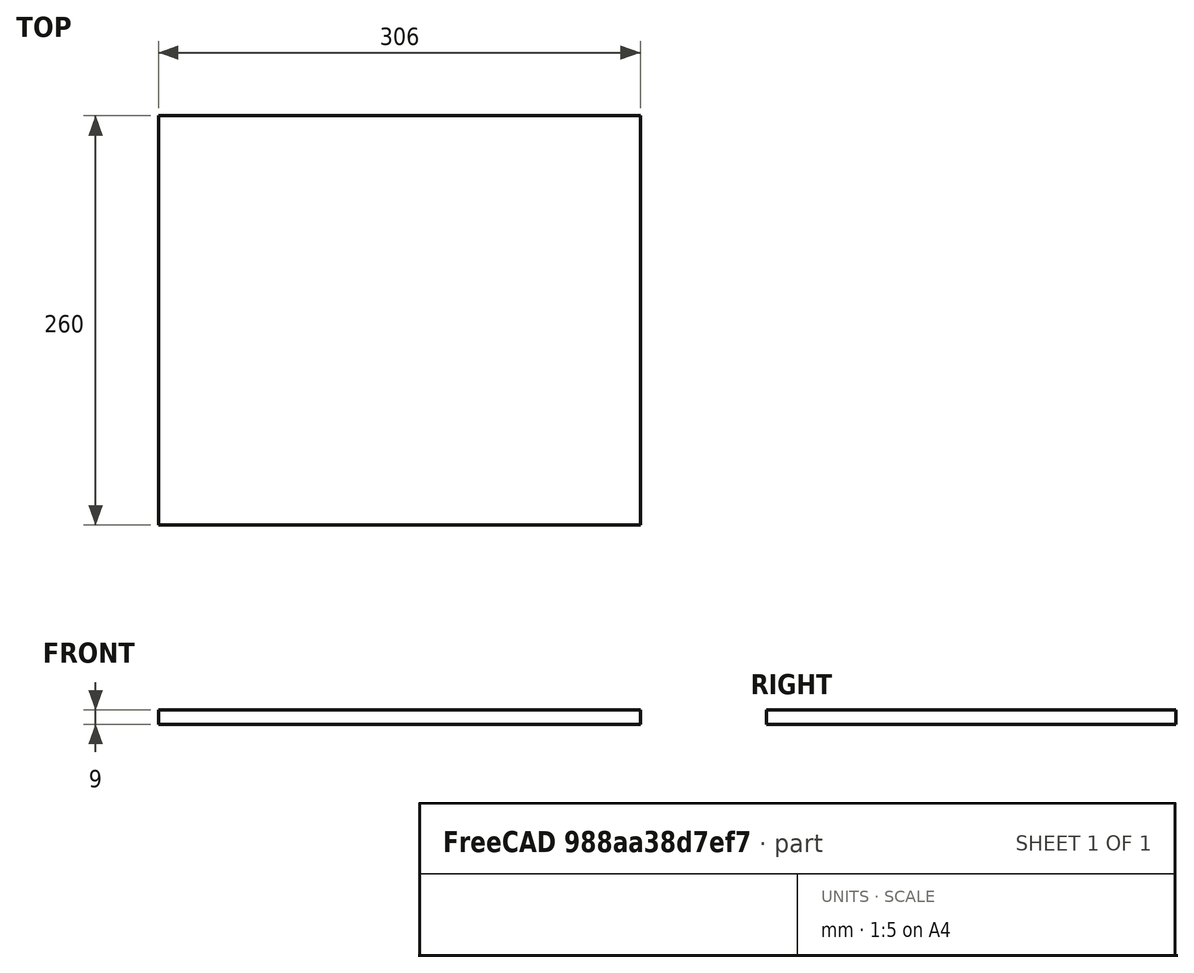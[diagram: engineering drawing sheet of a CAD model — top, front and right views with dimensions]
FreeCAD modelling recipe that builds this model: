
FCSTD DOCUMENT  (FreeCAD 0.16RUnknown)
Label: plaque_av
License: All rights reserved
LicenseURL: http://en.wikipedia.org/wiki/All_rights_reserved
objects: App::FeaturePython×2, Drawing::FeatureViewPart×2, Part::Plane×1, Part::FeaturePython×1, Part::Extrusion×1, App::DocumentObjectGroup×1, Drawing::FeatureViewPython×1, Drawing::FeaturePage×1
note: 3 computed .brp shape members not serialized (recipe doc carries the construction recipe); baked Part::Feature solids carry a one-line shape summary decoded from their .brp

FEATURE [Part::Plane] square
  Length = 306
  Placement = pos=(20,-130,0) rot=(0,0,1;0rad)
  Width = 260
FEATURE [Part::FeaturePython] RefineLinearExtrude  # WARN: FeaturePython — macro-defined, semantics opaque (R4)
  Base = -> square
FEATURE [Part::Extrusion] LinearExtrude
  Base = -> RefineLinearExtrude
  Dir = (0,0,9)
  Solid = true
FEATURE [App::FeaturePython] Dimension  # Draft dimension (typed FeaturePython)
  Dimline = (0,139,0)
  Direction = (0,0,0)
  Distance = 306
  End = (326,130,0)
  Normal = (0,0,1)
  Start = (20,130,0)
FEATURE [App::FeaturePython] Dimension001  # Draft dimension (typed FeaturePython)
  Dimline = (8,0,0)
  Direction = (0,0,0)
  Distance = 260
  End = (20,-130,0)
  Normal = (0,0,1)
  Start = (20,130,0)
FEATURE [App::DocumentObjectGroup] Groupe  label="Dimensions XY"
  Group = -> [Dimension,Dimension001]
FEATURE [Drawing::FeatureViewPython] ViewGroupe  # drawing view (typed FeaturePython)
  Direction = (0,0,0)
  FillStyle = 0
  FontSize = 12
  LineStyle = 0
  LineWidth = 0.35
  Rotation = -90
  Scale = 0.5
  Source = -> Groupe
  ViewResult = <g id="ViewGroupe" transform="rotate(-90.0,114.0,217.17) translate(114.0,217.17) scale(0.5,-0.5)"><path d="M 20.0 130.0 L 20.0 139.0 L 326.0 139.0 L 326.0 130.0" fill="none" stroke="#000000" stroke-width="0.7 px" style="stroke-width:0.7;stroke-miterlimit:4;stroke-dasharray:none" freecad:basepoint1="20.0 130.0" freecad:basepoint2="326.0 130.0" freecad:dimpoint="20.0 139.0"/>\n<path transform="rotate(-0.0,20.0,139.0) translate(20.0,139.0) scale(0.666666666667,0.666666666667)" freecad:skip="1" fill="#000000" stroke="none" style="stroke-miterlimit:4;stroke-dasharray:none" d="M 0 0 L 4 1 L 4 -1 Z"/>\n<path transform="rotate(180.0,326.0,139.0) translate(326.0,139.0) scale(0.666666666667,0.666666666667)" freecad:skip="1" fill="#000000" stroke="none" style="stroke-miterlimit:4;stroke-dasharray:none" d="M 0 0 L 4 1 L 4 -1 Z"/>\n<text fill="#000000" font-size="12.0" style="text-anchor:middle;text-align:center;font-family:" transform="rotate(-0.0,173.0,140.0) translate(173.0,140.0) scale(1,-1) " freecad:skip="1">\n306,00 </text>\n<path d="M 20.0 130.0 L 8.0 130.0 L 8.0 -130.0 L 20.0 -130.0" fill="none" stroke="#000000" stroke-width="0.7 px" style="stroke-width:0.7;stroke-miterlimit:4;stroke-dasharray:none" freecad:basepoint1="20.0 130.0" freecad:basepoint2="20.0 -130.0" freecad:dimpoint="8.0 130.0"/>\n<path transform="rotate(-90.0,8.0,130.0) translate(8.0,130.0) scale(0.666666666667,0.666666666667)" freecad:skip="1" fill="#000000" stroke="none" style="stroke-miterlimit:4;stroke-dasharray:none" d="M 0 0 L 4 1 L 4 -1 Z"/>\n<path transform="rotate(90.0,8.0,-130.0) translate(8.0,-130.0) scale(0.666666666667,0.666666666667)" freecad:skip="1" fill="#000000" stroke="none" style="stroke-miterlimit:4;stroke-dasharray:none" d="M 0 0 L 4 1 L 4 -1 Z"/>\n<text fill="#000000" font-size="12.0" style="text-anchor:middle;text-align:center;font-family:" transform="rotate(-90.0,9.0,0.0) translate(9.0,0.0) scale(1,-1) " freecad:skip="1">\n260,00 </text>\n</g>
  Visible = true
  X = 114
  Y = 217.17
FEATURE [Drawing::FeatureViewPart] Ortho001  label="Ortho_0_-1"
  Direction = (0,0,1)
  HiddenWidth = 0.15
  LineWidth = 0.35
  Rotation = 90
  Scale = 0.5
  ShowHiddenLines = false
  ShowSmoothLines = false
  Source = -> LinearExtrude
  Tolerance = 0.05
  ViewResult = <g id="Ortho_0_-1"\n   transform="rotate(90,114,44.17) translate(114,44.17) scale(0.5,0.5)"\n  >\n<g   stroke="rgb(0, 0, 0)"\n   stroke-width="0.7"\n   stroke-linecap="butt"\n   stroke-linejoin="miter"\n   fill="none"\n   transform="scale(1,-1)"\n  >\n<path id= "1" d=" M 20 -130 L 20 130 " />\n<path id= "2" d=" M 20 -130 L 326 -130 " />\n<path id= "3" d=" M 326 -130 L 326 130 " />\n<path id= "4" d=" M 20 130 L 326 130 " />\n</g>\n</g>
  Visible = true
  X = 114
  Y = 44.17
FEATURE [Drawing::FeatureViewPart] Ortho002  label="Ortho_1_-1"
  Direction = (0.57735,-0.57735,0.57735)
  HiddenWidth = 0.15
  LineWidth = 0.35
  Rotation = 60
  Scale = 0.5
  ShowHiddenLines = false
  ShowSmoothLines = false
  Source = -> LinearExtrude
  Tolerance = 0.05
  ViewResult = <g id="Ortho_1_-1"\n   transform="rotate(60,233.335,97.1903) translate(233.335,97.1903) scale(0.5,0.5)"\n  >\n<g   stroke="rgb(0, 0, 0)"\n   stroke-width="0.7"\n   stroke-linecap="butt"\n   stroke-linejoin="miter"\n   fill="none"\n   transform="scale(1,-1)"\n  >\n<path id= "1" d=" M 14.1421 -97.9796 L 7.77817 -94.3054 " />\n<path id= "2" d=" M 7.77817 -94.3054 L 7.77817 117.984 " />\n<path id= "3" d=" M 230.517 26.9444 L 224.153 30.6186 " />\n<path id= "4" d=" M 14.1421 -97.9796 L 230.517 26.9444 " />\n<path id= "5" d=" M 7.77817 -94.3054 L 224.153 30.6186 " />\n<path id= "6" d=" M 230.517 239.233 L 224.153 242.908 " />\n<path id= "7" d=" M 230.517 26.9444 L 230.517 239.233 " />\n<path id= "8" d=" M 224.153 30.6186 L 224.153 242.908 " />\n<path id= "9" d=" M 7.77817 117.984 L 224.153 242.908 " />\n</g>\n</g>
  Visible = true
  X = 233.335
  Y = 97.1903
FEATURE [Drawing::FeaturePage] Page
  EditableTexts = AUTHOR NAME | CREATION DATE | SUPERVISOR NAME | CHECK DATE | 0,5 | WEIGHT | NUMBER | SHEET | Caisse | Avant
  Group = -> [ViewGroupe,Ortho001,Ortho002]
